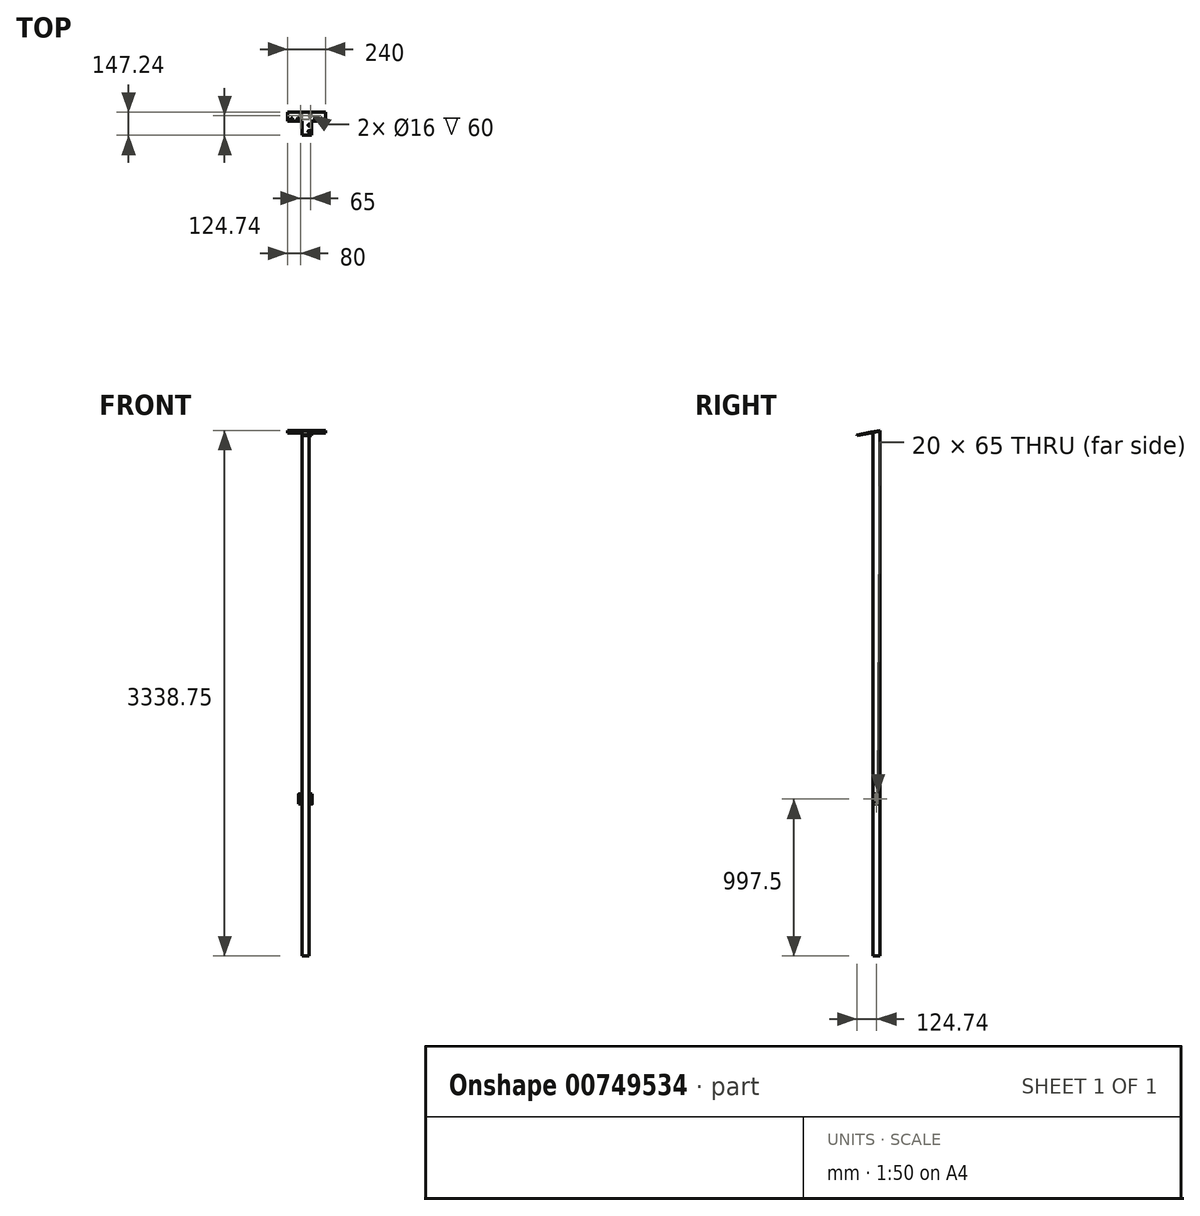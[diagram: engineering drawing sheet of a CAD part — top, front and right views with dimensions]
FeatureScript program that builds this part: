
annotation { "Feature Type Name" : "Feature", "Feature Type Description" : "" }
export const myFeature = defineFeature(function(context is Context, id is Id, definition is map)
    precondition{}
    {
        {
            var Q0;
            Q0=qCreatedBy(makeId("Top.planeOp"),FACE);
            var sketch = newSketch(context, id + "F0", { "sketchPlane" : qUnion([Q0])});
            skLineSegment(sketch, "E0.bottom", {"start": v(22.5, -22.5) * mm, "end": v(-22.5, -22.5) * mm});
            skLineSegment(sketch, "E0.top", {"start": v(22.5, 22.5) * mm, "end": v(-22.5, 22.5) * mm});
            skLineSegment(sketch, "E0.left", {"start": v(22.5, -22.5) * mm, "end": v(22.5, 22.5) * mm});
            skLineSegment(sketch, "E0.right", {"start": v(-22.5, -22.5) * mm, "end": v(-22.5, 22.5) * mm});
            skPoint(sketch, "E0.middle", {"position": v(0, 0) * mm});
            skSolve(sketch);
        }
        {
            var Q0;
            Q0=qSketchRegion(id+"F0",true);
            extrude(context, id + "F1", {"entities" : qUnion([Q0]), "depth" : 3330 * mm, "offsetDistance" : 25 * mm});
        }
        {
            var Q0;
            Q0=qCreatedBy(makeId("Top.planeOp"),FACE);
            cPlane(context, id + "F2", {"entities" : qUnion([Q0]), "cplaneType" : CPlaneType.OFFSET, "offset" : 965 * mm, "width" : 150 * mm, "height" : 150 * mm});
        }
        {
            var Q0;
            Q0=qCreatedBy(id+"F2.planeOp",FACE);
            var sketch = newSketch(context, id + "F3", { "sketchPlane" : qUnion([Q0])});
            skLineSegment(sketch, "E1", {"start": v(0, 0) * mm, "end": v(22.5, 0) * mm});
            skLineSegment(sketch, "E2", {"start": v(22.5, 0) * mm, "end": v(32.5, 0) * mm});
            skCircle(sketch, "E3", {"center": v(32.5, 0) * mm, "radius": 10 * mm});
            skLineSegment(sketch, "E4", {"start": v(32.5, 0) * mm, "end": v(32.5, 2) * mm});
            skLineSegment(sketch, "E5", {"start": v(32.5, 0) * mm, "end": v(32.5, -2) * mm});
            skLineSegment(sketch, "E6", {"start": v(32.5, -2) * mm, "end": v(22.5, -2) * mm});
            skLineSegment(sketch, "E7", {"start": v(32.5, 2) * mm, "end": v(22.5, 2) * mm});
            skLineSegment(sketch, "E8", {"start": v(0, 0) * mm, "end": v(-22.5, 0) * mm});
            skLineSegment(sketch, "E9", {"start": v(-22.5, 0) * mm, "end": v(-32.5, 0) * mm});
            skCircle(sketch, "E10", {"center": v(-32.5, 0) * mm, "radius": 10 * mm});
            skLineSegment(sketch, "E11", {"start": v(32.5, 2) * mm, "end": v(32.5, 10) * mm});
            skLineSegment(sketch, "E12", {"start": v(32.5, 10) * mm, "end": v(-32.5, 10) * mm});
            skLineSegment(sketch, "E13", {"start": v(-32.5, 10) * mm, "end": v(-32.5, -10) * mm});
            skLineSegment(sketch, "E14", {"start": v(-32.5, -10) * mm, "end": v(32.5, -10) * mm});
            skSolve(sketch);
        }
        {
            var Q0;
            Q0=qSketchRegion(id+"F3",true);
            var Q1;
            {var subQ0=sQuery(id+"F3.wireOp",EDGE,"E2");Q1=makeQuery(id+"F3.imprint","IMPRINT",FACE,{"disambiguationData":[TD([[makeQuery(id+"F3.imprint","IMPRINT",EDGE,{"derivedFrom":subQ0}),1.0]])]});}
            var Q2;
            {var subQ0=sQuery(id+"F3.wireOp",EDGE,"E2");Q2=makeQuery(id+"F3.imprint","IMPRINT",FACE,{"disambiguationData":[TD([[makeQuery(id+"F3.imprint","IMPRINT",EDGE,{"derivedFrom":subQ0}),-1.0]])]});}
            extrude(context, id + "F4", {"entities" : qUnion([Q0, Q1, Q2]), "operationType" : NewBodyOperationType.ADD, "depth" : 5 * mm, "offsetDistance" : 25 * mm});
        }
        {
            var Q0;
            Q0=makeQuery(id+"F4.opExtrude","CAP_FACE",FACE,{"disambiguationData":[OSD([sQuery(id+"F3.wireOp",EDGE,"E3")])],"isStart":false});
            var sketch = newSketch(context, id + "F5", { "sketchPlane" : qUnion([Q0])});
            skCircle(sketch, "E15", {"center": v(32.5, 0) * mm, "radius": 10 * mm});
            skCircle(sketch, "E16", {"center": v(32.5, 0) * mm, "radius": 8 * mm});
            skCircle(sketch, "E17", {"center": v(-32.5, 0) * mm, "radius": 8 * mm});
            skCircle(sketch, "E18", {"center": v(-32.5, 0) * mm, "radius": 10 * mm});
            skLineSegment(sketch, "E19.0", {"start": v(-32.5, -10) * mm, "end": v(-22.5, -10) * mm});
            skLineSegment(sketch, "E20.0", {"start": v(-22.5, -10) * mm, "end": v(-22.5, 10) * mm});
            skLineSegment(sketch, "E21.0", {"start": v(-22.5, 10) * mm, "end": v(-32.5, 10) * mm});
            skLineSegment(sketch, "E22.0", {"start": v(22.5, -10) * mm, "end": v(32.5, -10) * mm});
            skPoint(sketch, "E23.0", {"position": v(22.5, 0) * mm});
            skLineSegment(sketch, "E24.0", {"start": v(22.5, -10) * mm, "end": v(22.5, 10) * mm});
            skLineSegment(sketch, "E25.0", {"start": v(22.5, 10) * mm, "end": v(22.5, 10) * mm});
            skLineSegment(sketch, "E26.0", {"start": v(32.5, 10) * mm, "end": v(22.5, 10) * mm});
            skSolve(sketch);
        }
        {
            var Q0;
            Q0=makeQuery(id+"F5.imprint","IMPRINT",FACE,{"disambiguationData":[TD([[makeQuery(id+"F5.imprint","IMPRINT",EDGE,{"derivedFrom":sQuery(id+"F5.wireOp",EDGE,"E15")}),1.0]])]});
            var Q1;
            Q1=makeQuery(id+"F5.imprint","IMPRINT",FACE,{"disambiguationData":[TD([[makeQuery(id+"F5.imprint","IMPRINT",EDGE,{"derivedFrom":sQuery(id+"F5.wireOp",EDGE,"E17")}),-1.0]])]});
            var Q2;
            {var subQ0=sQuery(id+"F5.wireOp",EDGE,"E22.0");Q2=makeQuery(id+"F5.imprint","IMPRINT",FACE,{"disambiguationData":[TD([[makeQuery(id+"F5.imprint","IMPRINT",EDGE,{"derivedFrom":subQ0}),1.0]])]});}
            var Q3;
            {var subQ0=sQuery(id+"F5.wireOp",EDGE,"E26.0");Q3=makeQuery(id+"F5.imprint","IMPRINT",FACE,{"disambiguationData":[TD([[makeQuery(id+"F5.imprint","IMPRINT",EDGE,{"derivedFrom":subQ0}),1.0]])]});}
            var Q4;
            {var subQ0=sQuery(id+"F5.wireOp",EDGE,"E21.0");Q4=makeQuery(id+"F5.imprint","IMPRINT",FACE,{"disambiguationData":[TD([[makeQuery(id+"F5.imprint","IMPRINT",EDGE,{"derivedFrom":subQ0}),1.0]])]});}
            var Q5;
            {var subQ0=sQuery(id+"F5.wireOp",EDGE,"E19.0");Q5=makeQuery(id+"F5.imprint","IMPRINT",FACE,{"disambiguationData":[TD([[makeQuery(id+"F5.imprint","IMPRINT",EDGE,{"derivedFrom":subQ0}),1.0]])]});}
            extrude(context, id + "F6", {"entities" : qUnion([Q0, Q1, Q2, Q3, Q4, Q5]), "operationType" : NewBodyOperationType.ADD, "depth" : 60 * mm, "offsetDistance" : 25 * mm});
        }
        {
            var Q0;
            Q0=makeQuery(id+"F1.opExtrude","CAP_EDGE",EDGE,{"disambiguationData":[OSD([sQuery(id+"F0.wireOp",EDGE,"E0.bottom")])],"isStart":false});
            cPlane(context, id + "F7", {"entities" : qUnion([Q0]), "cplaneType" : CPlaneType.LINE_ANGLE, "offset" : 25 * mm, "angle" : 101 * degree, "oppositeDirection" : true, "width" : 150 * mm, "height" : 150 * mm});
        }
        {
            var Q0;
            Q0=makeQuery(id+"F1.opExtrude","CAP_FACE",FACE,{"disambiguationData":[OSD([sQuery(id+"F0.wireOp",EDGE,"E0.bottom"),sQuery(id+"F0.wireOp",EDGE,"E0.top"),sQuery(id+"F0.wireOp",EDGE,"E0.left"),sQuery(id+"F0.wireOp",EDGE,"E0.right")])],"isStart":false});
            var sketch = newSketch(context, id + "F8", { "sketchPlane" : qUnion([Q0])});
            skLineSegment(sketch, "E27.bottom", {"start": v(-22.5, 22.5) * mm, "end": v(22.5, 22.5) * mm});
            skLineSegment(sketch, "E27.top", {"start": v(-22.5, -22.5) * mm, "end": v(22.5, -22.5) * mm});
            skLineSegment(sketch, "E27.left", {"start": v(-22.5, 22.5) * mm, "end": v(-22.5, -22.5) * mm});
            skLineSegment(sketch, "E27.right", {"start": v(22.5, 22.5) * mm, "end": v(22.5, -22.5) * mm});
            skSolve(sketch);
        }
        {
            var Q0;
            Q0=qCreatedBy(id+"F7.planeOp",FACE);
            var sketch = newSketch(context, id + "F9", { "sketchPlane" : qUnion([Q0])});
            skLineSegment(sketch, "E28.bottom", {"start": v(-22.5, -659.15) * mm, "end": v(22.5, -659.15) * mm});
            skLineSegment(sketch, "E28.top", {"start": v(-22.5, -613.3) * mm, "end": v(22.5, -613.3) * mm});
            skLineSegment(sketch, "E28.left", {"start": v(-22.5, -659.15) * mm, "end": v(-22.5, -613.3) * mm});
            skLineSegment(sketch, "E28.right", {"start": v(22.5, -659.15) * mm, "end": v(22.5, -613.3) * mm});
            skSolve(sketch);
        }
        {
            var Q0;
            Q0=makeQuery(id+"F9.imprint","IMPRINT",FACE,{"disambiguationData":[TD([[makeQuery(id+"F9.imprint","IMPRINT",EDGE,{"derivedFrom":sQuery(id+"F9.wireOp",EDGE,"E28.bottom")}),1.0]])]});
            extrude(context, id + "F10", {"entities" : qUnion([Q0]), "operationType" : NewBodyOperationType.ADD, "depth" : 25 * mm, "offsetDistance" : 25 * mm});
        }
        {
            var Q0;
            Q0=qCreatedBy(id+"F7.planeOp",FACE);
            var sketch = newSketch(context, id + "F11", { "sketchPlane" : qUnion([Q0])});
            skLineSegment(sketch, "E29.bottom", {"start": v(-22.5, -659.15) * mm, "end": v(37.5, -659.15) * mm});
            skLineSegment(sketch, "E29.top", {"start": v(-22.5, -599.15) * mm, "end": v(37.5, -599.15) * mm});
            skLineSegment(sketch, "E29.left", {"start": v(-22.5, -659.15) * mm, "end": v(-22.5, -599.15) * mm});
            skLineSegment(sketch, "E29.right", {"start": v(37.5, -659.15) * mm, "end": v(37.5, -599.15) * mm});
            skLineSegment(sketch, "E30.bottom", {"start": v(37.5, -659.15) * mm, "end": v(127.5, -659.15) * mm});
            skLineSegment(sketch, "E30.top", {"start": v(37.5, -599.15) * mm, "end": v(127.5, -599.15) * mm});
            skLineSegment(sketch, "E30.right", {"start": v(127.5, -659.15) * mm, "end": v(127.5, -599.15) * mm});
            skLineSegment(sketch, "E31.top", {"start": v(-22.5, -509.15) * mm, "end": v(37.5, -509.15) * mm});
            skLineSegment(sketch, "E31.left", {"start": v(-22.5, -599.15) * mm, "end": v(-22.5, -509.15) * mm});
            skLineSegment(sketch, "E31.right", {"start": v(37.5, -599.15) * mm, "end": v(37.5, -509.15) * mm});
            skLineSegment(sketch, "E32", {"start": v(-22.5, -659.15) * mm, "end": v(-22.5, -509.15) * mm});
            skLineSegment(sketch, "E33", {"start": v(-22.5, -659.15) * mm, "end": v(-112.5, -659.15) * mm});
            skLineSegment(sketch, "E34", {"start": v(-112.5, -659.15) * mm, "end": v(-112.5, -599.15) * mm});
            skLineSegment(sketch, "E35", {"start": v(-112.5, -599.15) * mm, "end": v(-22.5, -599.15) * mm});
            skSolve(sketch);
        }
        {
            var Q0;
            Q0=qSketchRegion(id+"F11",true);
            extrude(context, id + "F12", {"entities" : qUnion([Q0]), "operationType" : NewBodyOperationType.ADD, "depth" : 5 * mm, "offsetDistance" : 25 * mm});
        }
        {
            var Q0;
            Q0=makeQuery(id+"F12.boolean.opBoolean","MERGE",FACE,{"derivedFrom":[makeQuery(id+"F10.opExtrude","CAP_FACE",FACE,{"disambiguationData":[OSD([sQuery(id+"F9.wireOp",EDGE,"E28.bottom"),sQuery(id+"F9.wireOp",EDGE,"E28.top"),sQuery(id+"F9.wireOp",EDGE,"E28.left"),sQuery(id+"F9.wireOp",EDGE,"E28.right")])],"isStart":true}),makeQuery(id+"F12.opExtrude","CAP_FACE",FACE,{"disambiguationData":[OSD([sQuery(id+"F11.wireOp",EDGE,"E29.bottom"),sQuery(id+"F11.wireOp",EDGE,"E30.bottom"),sQuery(id+"F11.wireOp",EDGE,"E30.top"),sQuery(id+"F11.wireOp",EDGE,"E30.right"),sQuery(id+"F11.wireOp",EDGE,"E31.top"),sQuery(id+"F11.wireOp",EDGE,"E31.right"),sQuery(id+"F11.wireOp",EDGE,"E32")])],"isStart":true})]});
            var sketch = newSketch(context, id + "F13", { "sketchPlane" : qUnion([Q0])});
            skLineSegment(sketch, "E36", {"start": v(37.5, 509.15) * mm, "end": v(37.5, 534.15) * mm});
            skLineSegment(sketch, "E37", {"start": v(37.5, 534.15) * mm, "end": v(22.5, 534.15) * mm});
            skLineSegment(sketch, "E38", {"start": v(22.5, 534.15) * mm, "end": v(22.5, 574.15) * mm});
            skLineSegment(sketch, "E39", {"start": v(127.5, 599.15) * mm, "end": v(102.5, 599.15) * mm});
            skLineSegment(sketch, "E40", {"start": v(102.5, 599.15) * mm, "end": v(102.5, 614.15) * mm});
            skLineSegment(sketch, "E41", {"start": v(102.5, 614.15) * mm, "end": v(62.5, 614.15) * mm});
            skCircle(sketch, "E42", {"center": v(102.5, 614.15) * mm, "radius": 6 * mm});
            skCircle(sketch, "E43", {"center": v(62.5, 614.15) * mm, "radius": 6 * mm});
            skLineSegment(sketch, "E44", {"start": v(7.5, 509.15) * mm, "end": v(7.5, 602.33) * mm});
            skCircle(sketch, "E45.MirrorC", {"center": v(-47.5, 614.15) * mm, "radius": 6 * mm});
            skCircle(sketch, "E46.MirrorC", {"center": v(-87.5, 614.15) * mm, "radius": 6 * mm});
            skCircle(sketch, "E47.MirrorC", {"center": v(22.5, 534.15) * mm, "radius": 6 * mm});
            skCircle(sketch, "E48.MirrorC", {"center": v(22.5, 574.15) * mm, "radius": 6 * mm});
            skSolve(sketch);
        }
        {
            var Q0;
            Q0=qSketchRegion(id+"F13",true);
            extrude(context, id + "F14", {"entities" : qUnion([Q0]), "operationType" : NewBodyOperationType.REMOVE, "oppositeDirection" : true, "depth" : 25 * mm, "offsetDistance" : 25 * mm});
        }
        {
            var Q0;
            Q0=qCreatedBy(makeId("Top.planeOp"),FACE);
            var sketch = newSketch(context, id + "F15", { "sketchPlane" : qUnion([Q0])});
            skLineSegment(sketch, "E49.bottom", {"start": v(-22.5, 22.5) * mm, "end": v(127.5, 22.5) * mm});
            skLineSegment(sketch, "E49.top", {"start": v(-22.5, 27.27) * mm, "end": v(127.5, 27.27) * mm});
            skLineSegment(sketch, "E49.left", {"start": v(-22.5, 22.5) * mm, "end": v(-22.5, 27.27) * mm});
            skLineSegment(sketch, "E49.right", {"start": v(127.5, 22.5) * mm, "end": v(127.5, 27.27) * mm});
            skSolve(sketch);
        }
        {
            var Q0;
            Q0=qSketchRegion(id+"F15",true);
            extrude(context, id + "F16", {"entities" : qUnion([Q0]), "operationType" : NewBodyOperationType.REMOVE, "depth" : 3358.7 * mm, "offsetDistance" : 25 * mm});
        }
        {
            var Q0;
            Q0=makeQuery(id+"F16.boolean.opBoolean","COPY",FACE,{"derivedFrom":makeQuery(id+"F16.opExtrude","SWEPT_FACE",FACE,{"disambiguationData":[OSD([sQuery(id+"F15.wireOp",EDGE,"E49.left")])]})});
            var sketch = newSketch(context, id + "F17", { "sketchPlane" : qUnion([Q0])});
            skLineSegment(sketch, "E50", {"start": v(23.45, 3333.84) * mm, "end": v(22.5, 3333.65) * mm});
            skLineSegment(sketch, "E51", {"start": v(22.5, 3333.65) * mm, "end": v(22.5, 3338.75) * mm});
            skLineSegment(sketch, "E52", {"start": v(22.5, 3338.75) * mm, "end": v(23.45, 3333.84) * mm});
            skSolve(sketch);
        }
        {
            var Q0;
            Q0 = qSketchRegion(id + "F17", true);
            extrude(context, id + "F18", {"entities" : qUnion([Q0]), "operationType" : NewBodyOperationType.REMOVE, "oppositeDirection" : true, "depth" : 111 * mm, "offsetDistance" : 25 * mm});
        }
    });
